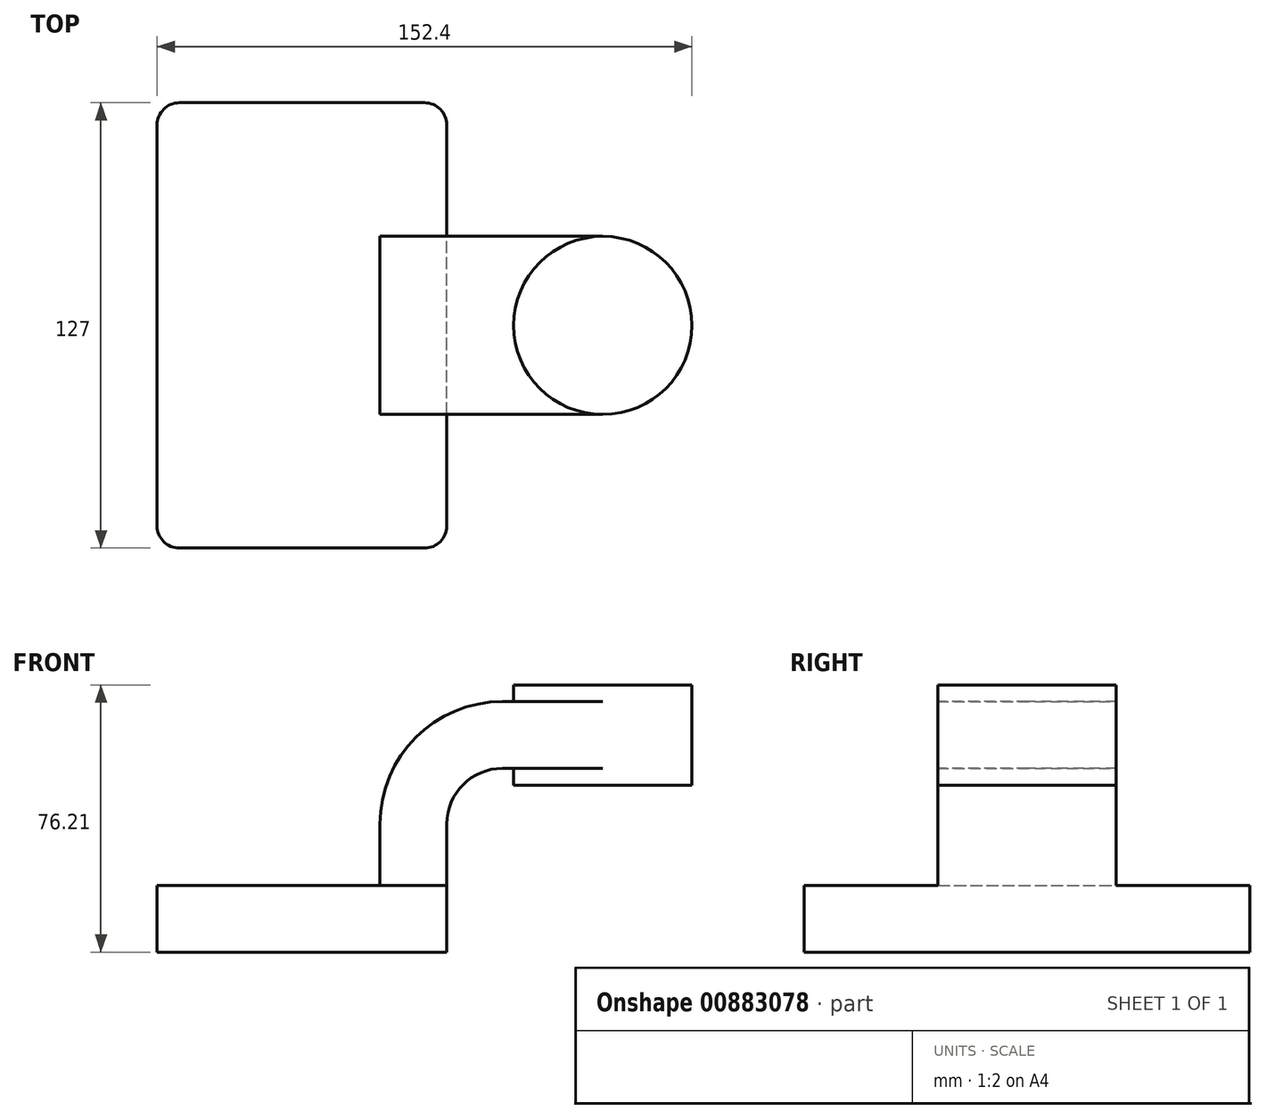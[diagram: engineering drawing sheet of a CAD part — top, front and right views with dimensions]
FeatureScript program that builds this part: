
annotation { "Feature Type Name" : "Feature", "Feature Type Description" : "" }
export const myFeature = defineFeature(function(context is Context, id is Id, definition is map)
    precondition{}
    {
        {
            var Q0;
            Q0=qCreatedBy(makeId("Front.planeOp"),FACE);
            var sketch = newSketch(context, id + "F0", { "sketchPlane" : qUnion([Q0])});
            skLineSegment(sketch, "E0.bottom", {"start": v(-41.28, -9.52) * mm, "end": v(41.28, -9.52) * mm});
            skLineSegment(sketch, "E0.top", {"start": v(-41.28, 9.53) * mm, "end": v(41.28, 9.53) * mm});
            skLineSegment(sketch, "E0.left", {"start": v(-41.27, -9.52) * mm, "end": v(-41.28, 9.53) * mm});
            skLineSegment(sketch, "E0.right", {"start": v(41.28, -9.52) * mm, "end": v(41.28, 9.53) * mm});
            skPoint(sketch, "E0.middle", {"position": v(0, 0) * mm});
            skLineSegment(sketch, "E1.bottom", {"start": v(60.33, 38.1) * mm, "end": v(111.12, 38.1) * mm});
            skLineSegment(sketch, "E1.top", {"start": v(60.33, 66.68) * mm, "end": v(111.12, 66.68) * mm});
            skLineSegment(sketch, "E1.left", {"start": v(60.33, 38.1) * mm, "end": v(60.33, 66.68) * mm});
            skLineSegment(sketch, "E1.right", {"start": v(111.12, 38.1) * mm, "end": v(111.12, 66.68) * mm});
            skPoint(sketch, "E1.middle", {"position": v(85.73, 52.39) * mm});
            skLineSegment(sketch, "E2", {"start": v(41.27, 9.53) * mm, "end": v(41.27, 27) * mm});
            skArc(sketch, "E3", {"start": v(41.27, 27) * mm, "mid": v(45.92, 38.23) * mm, "end": v(57.15, 42.88) * mm});
            skLineSegment(sketch, "E4", {"start": v(57.15, 42.88) * mm, "end": v(85.73, 42.88) * mm});
            skLineSegment(sketch, "E5.0", {"start": v(57.15, 61.93) * mm, "end": v(85.73, 61.93) * mm});
            skArc(sketch, "E5.1", {"start": v(22.23, 27) * mm, "mid": v(32.45, 51.7) * mm, "end": v(57.15, 61.93) * mm});
            skLineSegment(sketch, "E5.2", {"start": v(22.22, 9.53) * mm, "end": v(22.22, 27) * mm});
            skLineSegment(sketch, "E6", {"start": v(85.72, 38.1) * mm, "end": v(85.72, 66.68) * mm});
            skFitSpline(sketch, "E7", {"points": [v(-41.28, 9.53) * mm, v(57.15, 61.93) * mm], "startDerivative": vector(2.69, 106.65) * mm, "endDerivative": vector(171.45, -4.35) * mm});
            skSolve(sketch);
        }
        {
            var Q0;
            Q0=makeQuery(id+"F0.imprint","IMPRINT",FACE,{"disambiguationData":[TD([[makeQuery(id+"F0.imprint","IMPRINT",EDGE,{"derivedFrom":sQuery(id+"F0.wireOp",EDGE,"E0.bottom")}),1.0]])]});
            extrude(context, id + "F1", {"entities" : qUnion([Q0]), "endBound" : BoundingType.SYMMETRIC, "depth" : 127 * mm, "offsetDistance" : 25.4 * mm});
        }
        {
            var Q0;
            {var subQ0=sQuery(id+"F0.wireOp",EDGE,"E4");var subQ1=sQuery(id+"F0.wireOp",EDGE,"E1.left");var subQ2=makeQuery(id+"F0.imprint","INTERSECT",VERTEX,{"derivedFrom":[subQ1,subQ0]});Q0=makeQuery(id+"F0.imprint","IMPRINT",FACE,{"disambiguationData":[TD([[makeQuery(id+"F0.imprint","IMPRINT",EDGE,{"disambiguationData":[TD([[subQ2,-1.0]])],"derivedFrom":subQ1}),-1.0]])]});}
            var Q1;
            {var subQ1=sQuery(id+"F0.wireOp",EDGE,"E2");Q1=makeQuery(id+"F0.imprint","IMPRINT",FACE,{"disambiguationData":[TD([[makeQuery(id+"F0.imprint","IMPRINT",EDGE,{"derivedFrom":subQ1}),1.0]])]});}
            extrude(context, id + "F2", {"entities" : qUnion([Q0, Q1]), "operationType" : NewBodyOperationType.ADD, "endBound" : BoundingType.SYMMETRIC, "depth" : 50.8 * mm, "offsetDistance" : 25.4 * mm});
        }
        {
            var Q0;
            Q0=makeQuery(id+"F0.imprint","IMPRINT",FACE,{"disambiguationData":[TD([[makeQuery(id+"F0.imprint","IMPRINT",EDGE,{"derivedFrom":sQuery(id+"F0.wireOp",EDGE,"E5.1")}),1.0]])]});
            extrude(context, id + "F3", {"entities" : qUnion([Q0]), "operationType" : NewBodyOperationType.ADD, "endBound" : BoundingType.SYMMETRIC, "depth" : 15.88 * mm, "offsetDistance" : 25.4 * mm});
        }
        {
            var Q0;
            {var subQ0=sQuery(id+"F0.wireOp",EDGE,"E1.right");Q0=makeQuery(id+"F0.imprint","IMPRINT",FACE,{"disambiguationData":[TD([[makeQuery(id+"F0.imprint","IMPRINT",EDGE,{"derivedFrom":subQ0}),1.0]])]});}
            var Q1;
            Q1=sQuery(id+"F0.wireOp",EDGE,"E6");
            revolve(context, id + "F4", {"operationType" : NewBodyOperationType.ADD, "surfaceOperationType" : NewSurfaceOperationType.NEW, "entities" : qUnion([Q0]), "axis" : qUnion([Q1]), "revolveType" : RevolveType.FULL});
        }
        {
            var Q0;
            Q0=makeQuery(id+"F1.opExtrude","CAP_EDGE",EDGE,{"disambiguationData":[OSD([sQuery(id+"F0.wireOp",EDGE,"E0.right")])],"isStart":false});
            var Q1;
            Q1=makeQuery(id+"F1.opExtrude","CAP_EDGE",EDGE,{"disambiguationData":[OSD([sQuery(id+"F0.wireOp",EDGE,"E0.right")])],"isStart":true});
            var Q2;
            Q2=makeQuery(id+"F1.opExtrude","CAP_EDGE",EDGE,{"disambiguationData":[OSD([sQuery(id+"F0.wireOp",EDGE,"E0.left")])],"isStart":false});
            var Q3;
            Q3=makeQuery(id+"F1.opExtrude","CAP_EDGE",EDGE,{"disambiguationData":[OSD([sQuery(id+"F0.wireOp",EDGE,"E0.left")])],"isStart":true});
            fillet(context, id + "F5", {"entities" : qUnion([Q0, Q1, Q2, Q3]), "radius" : 6.35 * mm, "tangentPropagation" : true, "allowEdgeOverflow" : false});
        }
    });
